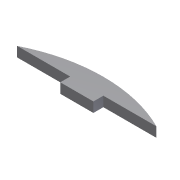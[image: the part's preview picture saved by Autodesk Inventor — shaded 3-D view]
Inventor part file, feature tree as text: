
AUTODESK INVENTOR PART (.ipt)
format: ipt  version: 2012 (Build 160160000, 160)  size: 73,216 bytes
history: native  units: mm
features: extrude x1, sketch x1
ambient origin geometry x8: Origin, YZ Plane, XZ Plane, XY Plane, X Axis, Y Axis, Z Axis, Center Point
bodies: Solid1 (feature_tree)
feature tree (2):
  extrude  "Extrusion1"  Depth=39.8mm
  sketch  "Sketch1"  dims[d0=94.0mm d1=39.8mm d2=3.0mm d3=10.0mm d4=5.0mm d5=3.0mm d6=0.0mm d8=16.0mm d9=16.0mm]
